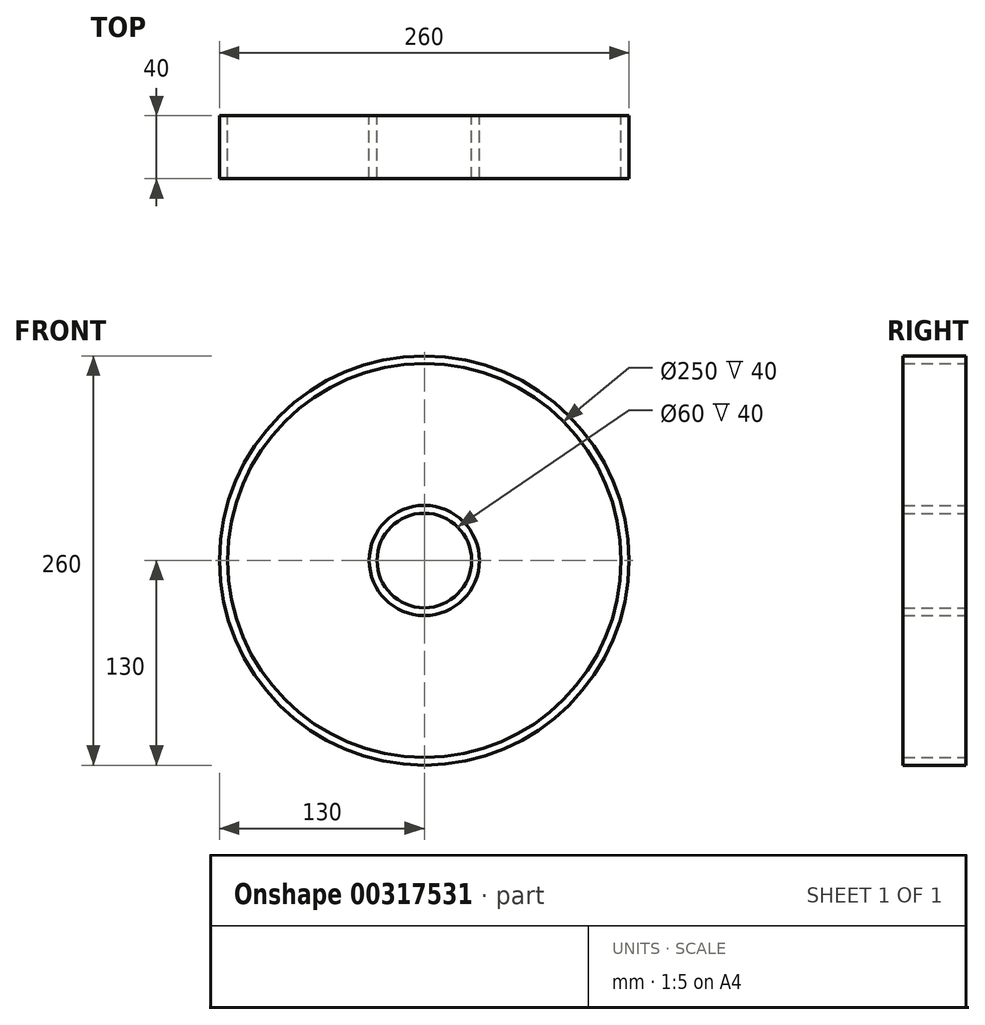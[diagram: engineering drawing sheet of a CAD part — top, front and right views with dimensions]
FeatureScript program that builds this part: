
annotation { "Feature Type Name" : "Feature", "Feature Type Description" : "" }
export const myFeature = defineFeature(function(context is Context, id is Id, definition is map)
    precondition{}
    {
        {
            var Q0;
            Q0=qCreatedBy(makeId("Front.planeOp"),FACE);
            var sketch = newSketch(context, id + "F0", { "sketchPlane" : qUnion([Q0])});
            skCircle(sketch, "E0", {"center": v(0, 0) * mm, "radius": 125 * mm});
            skCircle(sketch, "E1", {"center": v(0, 0) * mm, "radius": 30 * mm});
            skCircle(sketch, "E2.0", {"center": v(0, 0) * mm, "radius": 130 * mm});
            skCircle(sketch, "E3.0", {"center": v(0, 0) * mm, "radius": 35 * mm});
            skSolve(sketch);
        }
        {
            var Q0;
            Q0 = qSketchRegion(id + "F0", true);
            var Q1;
            Q1=makeQuery(id+"F0.imprint","IMPRINT",FACE,{"disambiguationData":[TD([[makeQuery(id+"F0.imprint","IMPRINT",EDGE,{"derivedFrom":sQuery(id+"F0.wireOp",EDGE,"E1")}),-1.0]])]});
            extrude(context, id + "F1", {"entities" : qUnion([Q0, Q1]), "depth" : 40 * mm});
        }
    });
